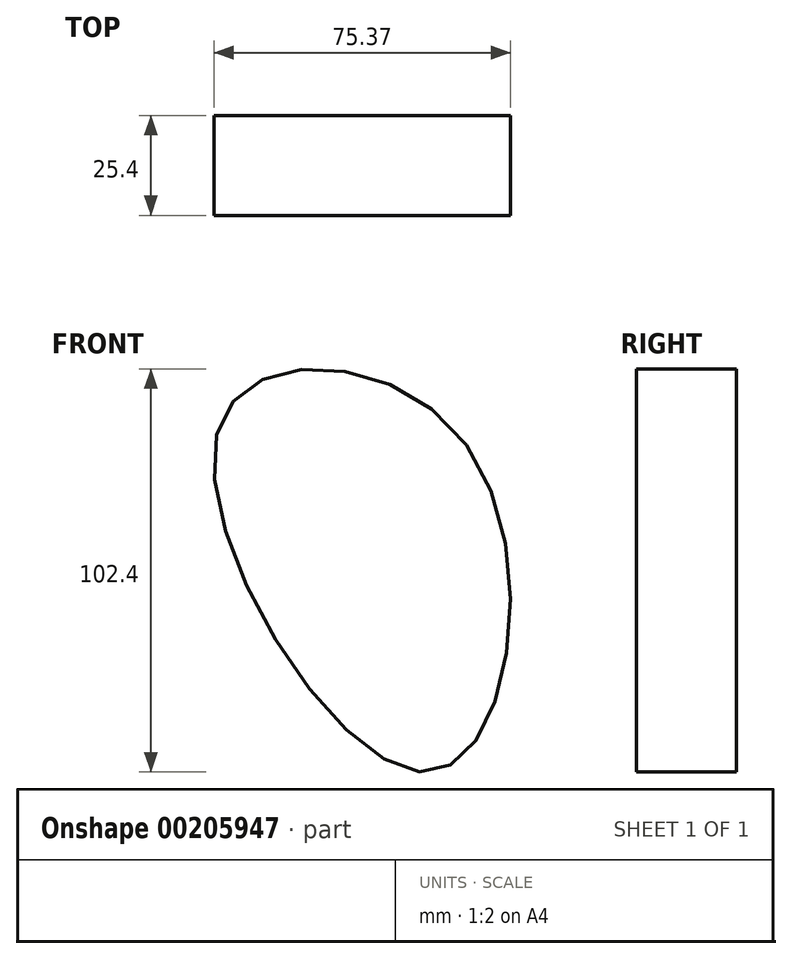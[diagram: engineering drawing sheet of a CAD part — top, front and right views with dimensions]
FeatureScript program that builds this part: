
annotation { "Feature Type Name" : "Feature", "Feature Type Description" : "" }
export const myFeature = defineFeature(function(context is Context, id is Id, definition is map)
    precondition{}
    {
        {
            var Q0;
            Q0=qCreatedBy(makeId("Front.planeOp"),FACE);
            var sketch = newSketch(context, id + "F0", { "sketchPlane" : qUnion([Q0])});
            skFitSpline(sketch, "E0", {"points": [v(20.96, 36.86) * mm, v(11.34, -46.23) * mm, v(-41.67, 42.29) * mm, v(20.96, 36.86) * mm]});
            skSolve(sketch);
        }
        {
            var Q0;
            Q0=makeQuery(id+"F0.imprint","IMPRINT",FACE,{"disambiguationData":[TD([[makeQuery(id+"F0.imprint","IMPRINT",EDGE,{"derivedFrom":sQuery(id+"F0.wireOp",EDGE,"E0")}),-1.0]])]});
            var Q1;
            Q1=sQuery(id+"F0.wireOp",EDGE,"E0");
            extrude(context, id + "F1", {"entities" : qUnion([Q0]), "surfaceEntities" : qUnion([Q1]), "depth" : 25.4 * mm});
        }
    });
